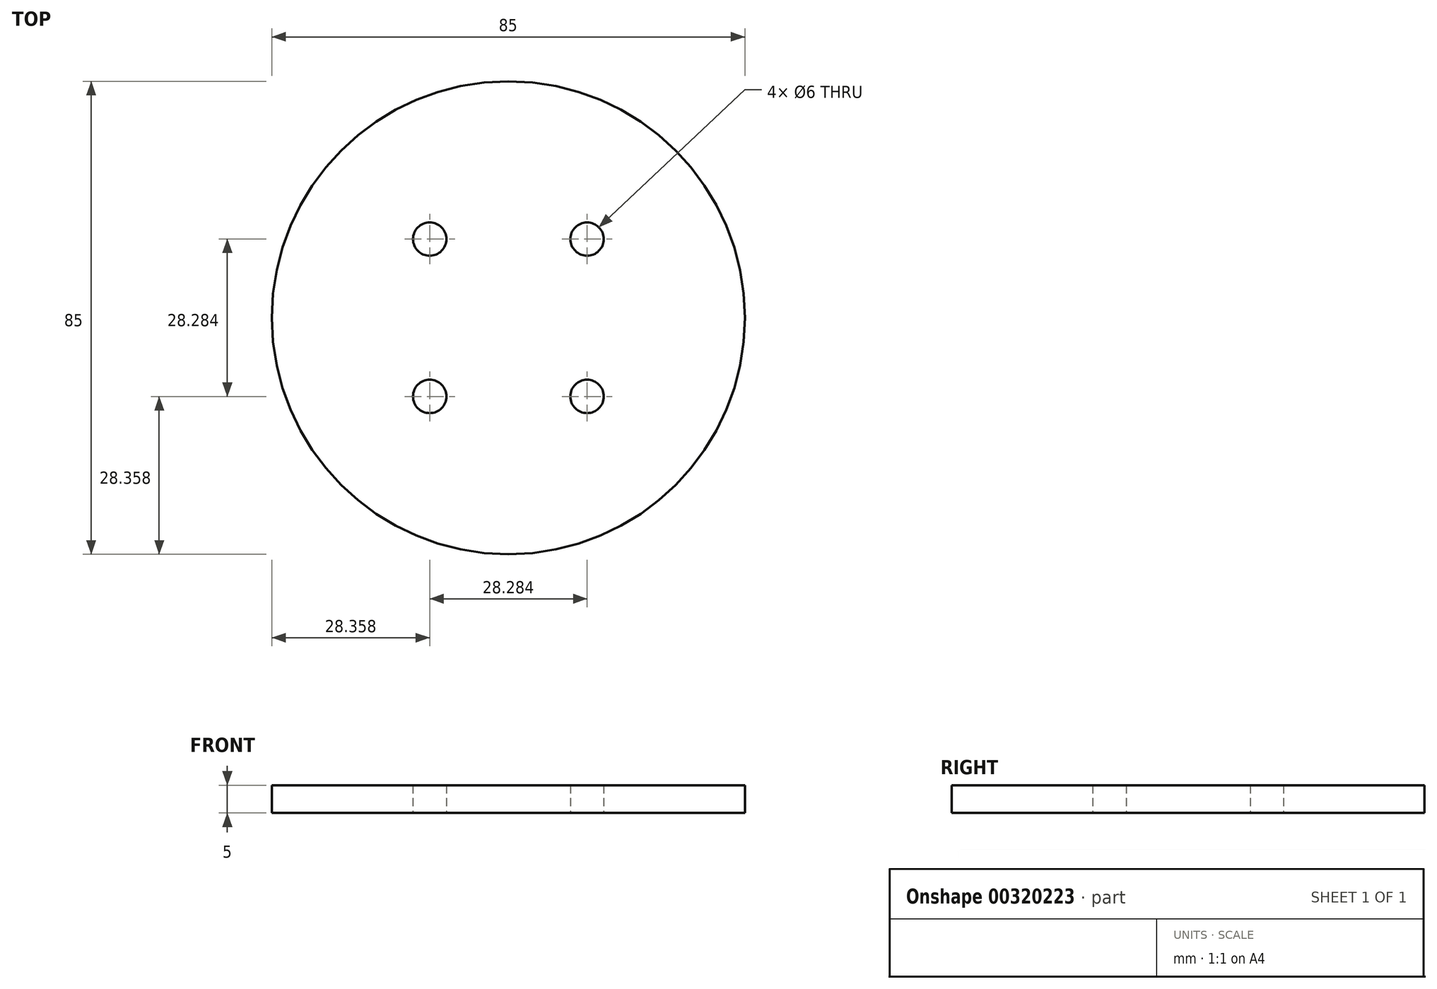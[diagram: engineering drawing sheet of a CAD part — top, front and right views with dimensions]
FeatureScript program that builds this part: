
annotation { "Feature Type Name" : "Feature", "Feature Type Description" : "" }
export const myFeature = defineFeature(function(context is Context, id is Id, definition is map)
    precondition{}
    {
        {
            var Q0;
            Q0=qCreatedBy(makeId("Top.planeOp"),FACE);
            var sketch = newSketch(context, id + "F0", { "sketchPlane" : qUnion([Q0])});
            skCircle(sketch, "E0", {"center": v(0, 0) * mm, "radius": 42.5 * mm});
            skCircle(sketch, "E1", {"center": v(0, 0) * mm, "radius": 20 * mm, "construction": true});
            skCircle(sketch, "E2", {"center": v(14.14, 14.14) * mm, "radius": 3 * mm});
            skCircle(sketch, "E3", {"center": v(14.14, -14.14) * mm, "radius": 3 * mm});
            skCircle(sketch, "E4", {"center": v(-14.14, -14.14) * mm, "radius": 3 * mm});
            skCircle(sketch, "E5", {"center": v(-14.14, 14.14) * mm, "radius": 3 * mm});
            skLineSegment(sketch, "E6", {"start": v(-14.14, 14.14) * mm, "end": v(14.14, 14.14) * mm, "construction": true});
            skLineSegment(sketch, "E7", {"start": v(14.14, -14.14) * mm, "end": v(14.14, 14.14) * mm, "construction": true});
            skSolve(sketch);
        }
        {
            var Q0;
            Q0=makeQuery(id+"F0.imprint","IMPRINT",FACE,{"disambiguationData":[TD([[makeQuery(id+"F0.imprint","IMPRINT",EDGE,{"derivedFrom":sQuery(id+"F0.wireOp",EDGE,"E0")}),1.0]])]});
            extrude(context, id + "F1", {"entities" : qUnion([Q0]), "depth" : 5 * mm});
        }
    });
